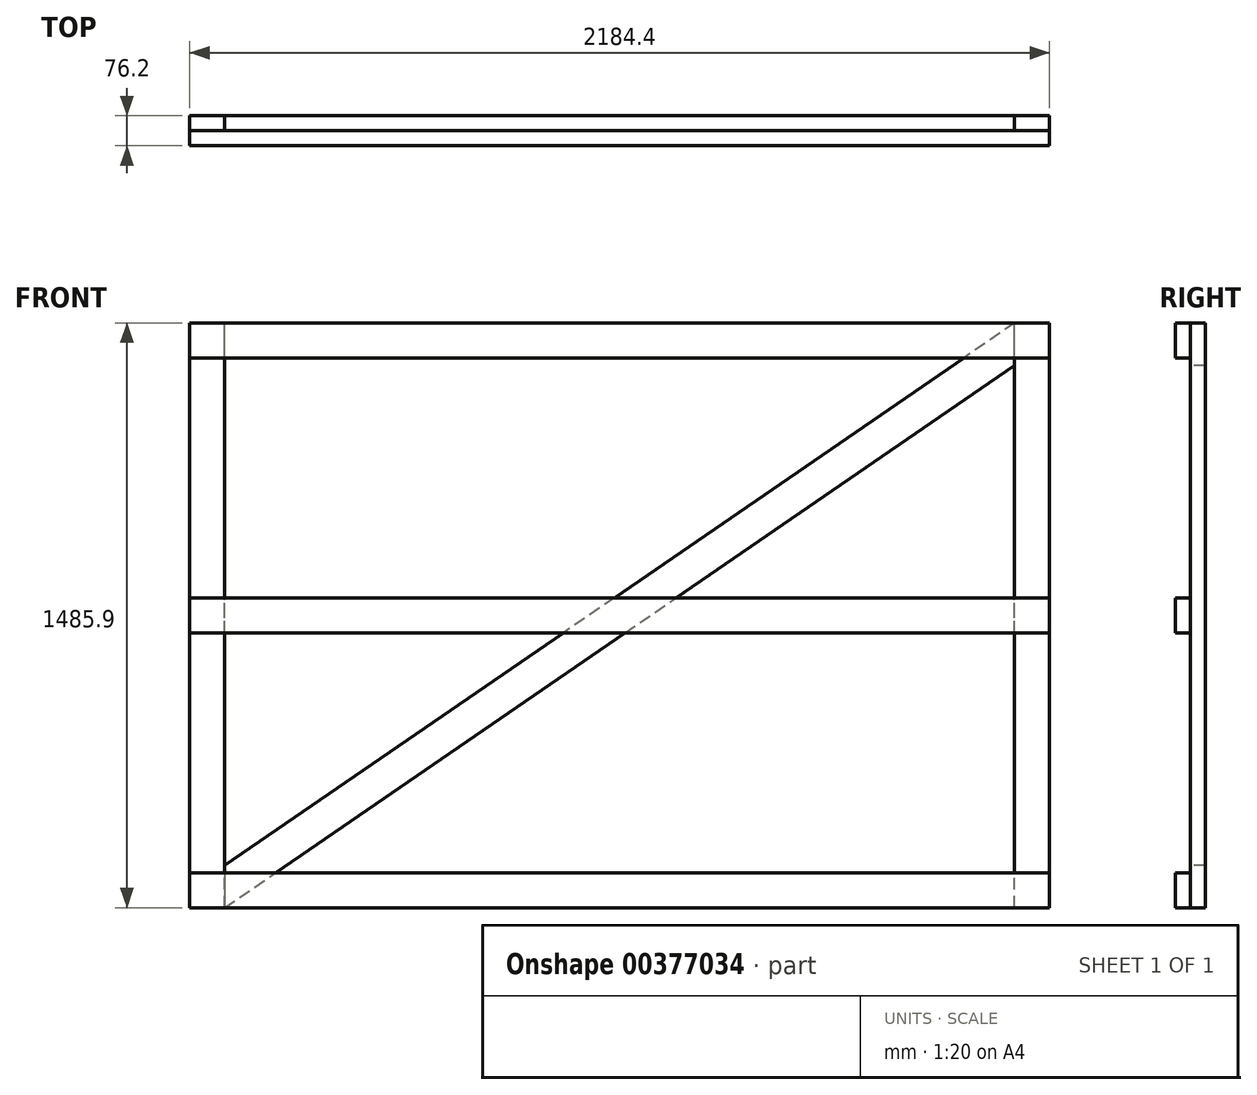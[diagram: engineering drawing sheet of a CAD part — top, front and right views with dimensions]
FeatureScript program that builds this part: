
annotation { "Feature Type Name" : "Feature", "Feature Type Description" : "" }
export const myFeature = defineFeature(function(context is Context, id is Id, definition is map)
    precondition{}
    {
        {
            var Q0;
            Q0=qCreatedBy(makeId("Right.planeOp"),FACE);
            var sketch = newSketch(context, id + "F0", { "sketchPlane" : qUnion([Q0])});
            skLineSegment(sketch, "E0.bottom", {"start": v(0, 233.45) * mm, "end": v(38.1, 233.45) * mm});
            skLineSegment(sketch, "E0.top", {"start": v(0, 144.55) * mm, "end": v(38.1, 144.55) * mm});
            skLineSegment(sketch, "E0.left", {"start": v(0, 233.45) * mm, "end": v(0, 144.55) * mm});
            skLineSegment(sketch, "E0.right", {"start": v(38.1, 233.45) * mm, "end": v(38.1, 144.55) * mm});
            skLineSegment(sketch, "E1.bottom", {"start": v(0, -465.05) * mm, "end": v(38.1, -465.05) * mm});
            skLineSegment(sketch, "E1.top", {"start": v(0, -553.95) * mm, "end": v(38.1, -553.95) * mm});
            skLineSegment(sketch, "E1.left", {"start": v(0, -465.05) * mm, "end": v(0, -553.95) * mm});
            skLineSegment(sketch, "E1.right", {"start": v(38.1, -465.05) * mm, "end": v(38.1, -553.95) * mm});
            skLineSegment(sketch, "E2.bottom", {"start": v(0, -1163.55) * mm, "end": v(38.1, -1163.55) * mm});
            skLineSegment(sketch, "E2.top", {"start": v(0, -1252.45) * mm, "end": v(38.1, -1252.45) * mm});
            skLineSegment(sketch, "E2.left", {"start": v(0, -1163.55) * mm, "end": v(0, -1252.45) * mm});
            skLineSegment(sketch, "E2.right", {"start": v(38.1, -1163.55) * mm, "end": v(38.1, -1252.45) * mm});
            skLineSegment(sketch, "E3", {"start": v(0, 144.55) * mm, "end": v(0, -465.05) * mm, "construction": true});
            skLineSegment(sketch, "E4", {"start": v(0, -553.95) * mm, "end": v(0, -1163.55) * mm, "construction": true});
            skSolve(sketch);
        }
        {
            var Q0;
            Q0 = qSketchRegion(id + "F0", true);
            extrude(context, id + "F1", {"entities" : qUnion([Q0]), "depth" : 2184.4 * mm});
        }
        {
            var Q0;
            Q0=makeQuery(id+"F1.opExtrude","SWEPT_FACE",FACE,{"disambiguationData":[OSD([sQuery(id+"F0.wireOp",EDGE,"E0.bottom")])]});
            var sketch = newSketch(context, id + "F2", { "sketchPlane" : qUnion([Q0])});
            skLineSegment(sketch, "E5.bottom", {"start": v(2184.4, 38.1) * mm, "end": v(2095.5, 38.1) * mm});
            skLineSegment(sketch, "E5.top", {"start": v(2184.4, 76.2) * mm, "end": v(2095.5, 76.2) * mm});
            skLineSegment(sketch, "E5.left", {"start": v(2184.4, 38.1) * mm, "end": v(2184.4, 76.2) * mm});
            skLineSegment(sketch, "E5.right", {"start": v(2095.5, 38.1) * mm, "end": v(2095.5, 76.2) * mm});
            skPoint(sketch, "E6.oppositeSnap0", {"position": v(2139.95, 76.2) * mm});
            skLineSegment(sketch, "E6.bottom", {"start": v(0, 38.1) * mm, "end": v(88.9, 38.1) * mm});
            skLineSegment(sketch, "E6.top", {"start": v(0, 76.2) * mm, "end": v(88.9, 76.2) * mm});
            skLineSegment(sketch, "E6.left", {"start": v(0, 38.1) * mm, "end": v(0, 76.2) * mm});
            skLineSegment(sketch, "E6.right", {"start": v(88.9, 38.1) * mm, "end": v(88.9, 76.2) * mm});
            skSolve(sketch);
        }
        {
            var Q0;
            Q0 = qSketchRegion(id + "F2", true);
            var Q1;
            Q1=makeQuery(id+"F1.opExtrude","SWEPT_FACE",FACE,{"disambiguationData":[OSD([sQuery(id+"F0.wireOp",EDGE,"E2.top")])]});
            extrude(context, id + "F3", {"entities" : qUnion([Q0]), "endBound" : BoundingType.UP_TO_SURFACE, "oppositeDirection" : true, "endBoundEntityFace" : qUnion([Q1]), "depth" : 1318.26 * mm});
        }
        {
            var Q0;
            Q0=makeQuery(id+"F1.opExtrude","SWEPT_FACE",FACE,{"disambiguationData":[OSD([sQuery(id+"F0.wireOp",EDGE,"E0.right")])]});
            var sketch = newSketch(context, id + "F4", { "sketchPlane" : qUnion([Q0])});
            skLineSegment(sketch, "E7", {"start": v(-2095.5, 233.45) * mm, "end": v(-88.9, -1144.6) * mm});
            skLineSegment(sketch, "E8", {"start": v(-88.9, -1144.6) * mm, "end": v(-88.9, -1252.45) * mm});
            skLineSegment(sketch, "E9", {"start": v(-88.9, -1252.45) * mm, "end": v(-2095.5, 125.6) * mm});
            skLineSegment(sketch, "E10", {"start": v(-2095.5, 125.6) * mm, "end": v(-2095.5, 233.45) * mm});
            skSolve(sketch);
        }
        {
            var Q0;
            Q0 = qSketchRegion(id + "F4", true);
            extrude(context, id + "F5", {"entities" : qUnion([Q0]), "depth" : 38.1 * mm});
        }
    });
